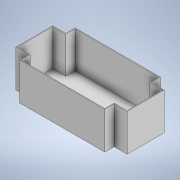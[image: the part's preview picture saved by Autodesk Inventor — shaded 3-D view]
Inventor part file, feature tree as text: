
AUTODESK INVENTOR PART (.ipt)
format: ipt  version: 2021 (Build 250183000, 183)  size: 151,552 bytes
history: native  units: mm
features: extrude x2, shell x2, sketch x2, plane x1, mirror x1
ambient origin geometry x8: Origin, YZ Plane, XZ Plane, XY Plane, X Axis, Y Axis, Z Axis, Center Point
bodies: Solid1 (feature_tree)
feature tree (8):
  extrude  "Extrusion1"  Depth=50.8mm
  extrude  "Extrusion2"  Depth=17.78mm
  shell  "Shell1"  Thickness=17.78mm
  plane  "Work Plane3"
  mirror  "Mirror2"
  shell  "Shell6"  Thickness=12.8mm
  sketch  "Sketch1"  dims[d0=152.4mm d1=50.8mm]
  sketch  "Sketch2"  dims[d4=38.1mm d5=0.0mm d6=17.78mm d7=17.78mm d8=12.8mm d9=0.0mm d10=1.0mm d140=37.1mm d141=1.0mm d109=0.5mm d110=0.872665mm d111=0.5mm d112=0.872665mm]
